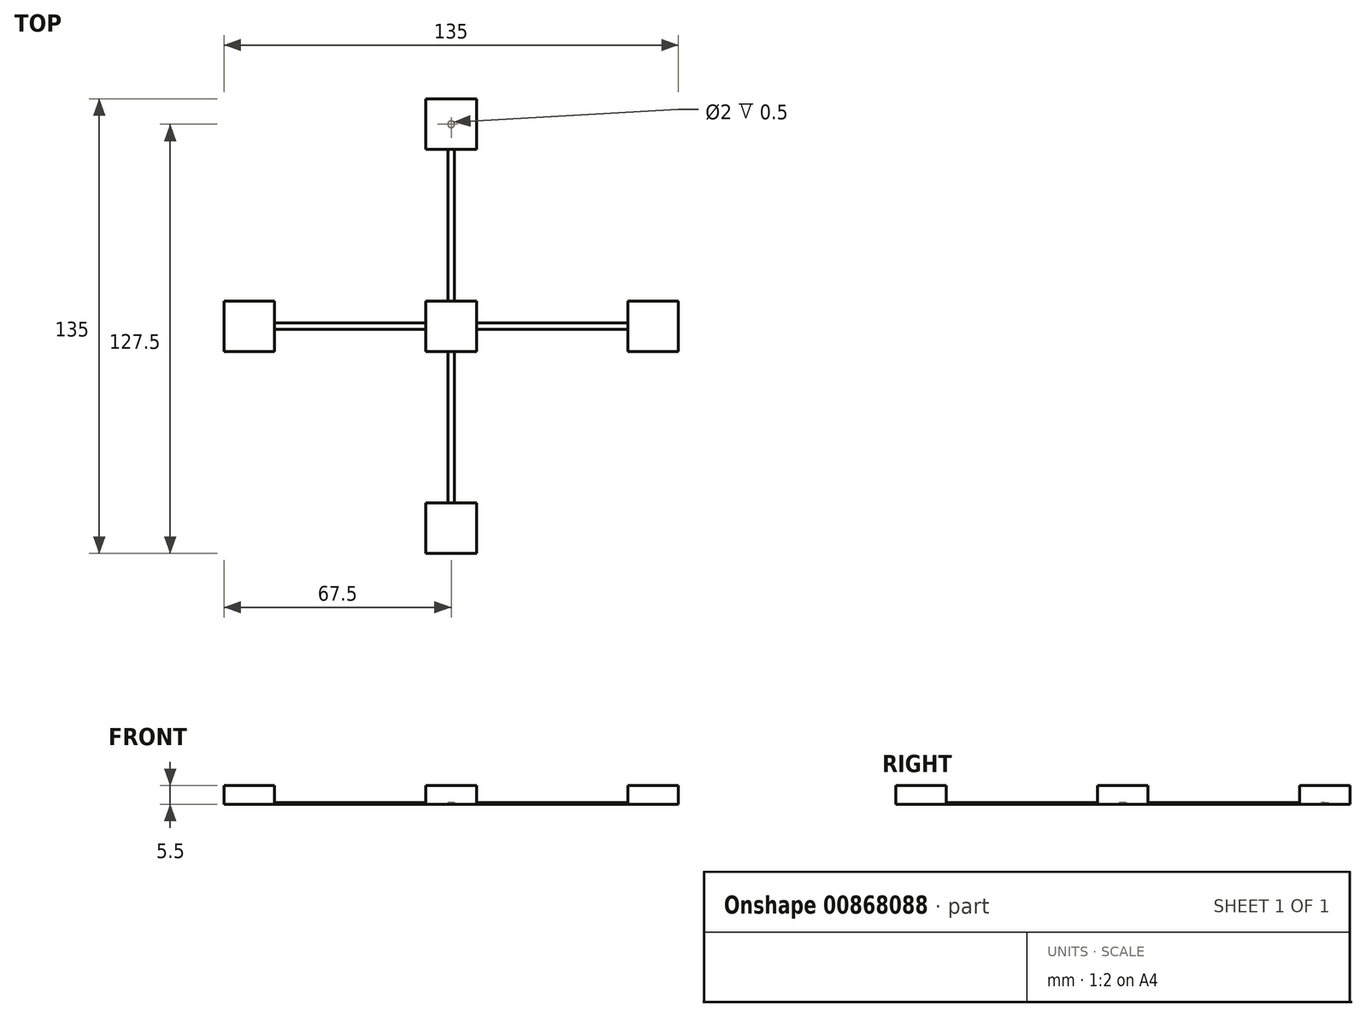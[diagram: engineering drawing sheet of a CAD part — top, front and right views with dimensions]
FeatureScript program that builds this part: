
annotation { "Feature Type Name" : "Feature", "Feature Type Description" : "" }
export const myFeature = defineFeature(function(context is Context, id is Id, definition is map)
    precondition{}
    {
        {
            var Q0;
            Q0=qCreatedBy(makeId("Top.planeOp"),FACE);
            var sketch = newSketch(context, id + "F0", { "sketchPlane" : qUnion([Q0])});
            skLineSegment(sketch, "E0.bottom", {"start": v(0, 0) * mm, "end": v(7.5, 0) * mm, "construction": true});
            skLineSegment(sketch, "E0.top", {"start": v(0, 7.5) * mm, "end": v(7.5, 7.5) * mm, "construction": true});
            skLineSegment(sketch, "E0.left", {"start": v(0, 0) * mm, "end": v(0, 7.5) * mm, "construction": true});
            skLineSegment(sketch, "E0.right", {"start": v(7.5, 0) * mm, "end": v(7.5, 7.5) * mm, "construction": true});
            skLineSegment(sketch, "E1.bottom", {"start": v(0, 67.5) * mm, "end": v(7.5, 67.5) * mm});
            skLineSegment(sketch, "E1.top", {"start": v(0, 52.5) * mm, "end": v(7.5, 52.5) * mm, "construction": true});
            skLineSegment(sketch, "E1.left", {"start": v(0, 67.5) * mm, "end": v(0, 52.5) * mm, "construction": true});
            skLineSegment(sketch, "E1.right", {"start": v(7.5, 67.5) * mm, "end": v(7.5, 52.5) * mm});
            skLineSegment(sketch, "E2", {"start": v(0, 0) * mm, "end": v(7.5, 7.5) * mm, "construction": true});
            skLineSegment(sketch, "E3", {"start": v(7.5, 52.5) * mm, "end": v(1, 52.5) * mm});
            skLineSegment(sketch, "E4", {"start": v(1, 52.5) * mm, "end": v(1, 7.5) * mm});
            skLineSegment(sketch, "E5", {"start": v(1, 7.5) * mm, "end": v(7.5, 7.5) * mm});
            skLineSegment(sketch, "E6.MirrorCS", {"start": v(52.5, 7.5) * mm, "end": v(52.5, 1) * mm});
            skLineSegment(sketch, "E7.MirrorCS", {"start": v(7.5, 1) * mm, "end": v(7.5, 7.5) * mm});
            skLineSegment(sketch, "E8.MirrorCS", {"start": v(52.5, 1) * mm, "end": v(7.5, 1) * mm});
            skLineSegment(sketch, "E9.MirrorCS", {"start": v(52.5, 0) * mm, "end": v(52.5, 7.5) * mm, "construction": true});
            skLineSegment(sketch, "E10.MirrorCS", {"start": v(67.5, 0) * mm, "end": v(52.5, 0) * mm, "construction": true});
            skLineSegment(sketch, "E11.MirrorCS", {"start": v(67.5, 7.5) * mm, "end": v(52.5, 7.5) * mm});
            skLineSegment(sketch, "E12.MirrorCS", {"start": v(67.5, 0) * mm, "end": v(67.5, 7.5) * mm});
            skLineSegment(sketch, "E13.1.0", {"start": v(0, 0) * mm, "end": v(-7.5, 7.5) * mm, "construction": true});
            skLineSegment(sketch, "E13.1.1", {"start": v(0, 52.5) * mm, "end": v(-7.5, 52.5) * mm, "construction": true});
            skLineSegment(sketch, "E13.1.2", {"start": v(-1, 52.5) * mm, "end": v(-1, 7.5) * mm});
            skLineSegment(sketch, "E13.1.3", {"start": v(0, 0) * mm, "end": v(-7.5, 0) * mm, "construction": true});
            skLineSegment(sketch, "E13.1.4", {"start": v(-67.5, 0) * mm, "end": v(-52.5, 0) * mm, "construction": true});
            skLineSegment(sketch, "E13.1.5", {"start": v(-52.5, 0) * mm, "end": v(-52.5, 7.5) * mm, "construction": true});
            skLineSegment(sketch, "E13.1.7", {"start": v(-7.5, 0) * mm, "end": v(-7.5, 7.5) * mm, "construction": true});
            skLineSegment(sketch, "E13.1.8", {"start": v(-52.5, 1) * mm, "end": v(-7.5, 1) * mm});
            skLineSegment(sketch, "E13.1.9", {"start": v(0, 7.5) * mm, "end": v(-7.5, 7.5) * mm, "construction": true});
            skLineSegment(sketch, "E13.1.10", {"start": v(0, 67.5) * mm, "end": v(-7.5, 67.5) * mm});
            skLineSegment(sketch, "E13.1.11", {"start": v(-7.5, 67.5) * mm, "end": v(-7.5, 52.5) * mm});
            skLineSegment(sketch, "E13.1.12", {"start": v(-67.5, 0) * mm, "end": v(-67.5, 7.5) * mm});
            skLineSegment(sketch, "E13.1.14", {"start": v(-67.5, 7.5) * mm, "end": v(-52.5, 7.5) * mm});
            skLineSegment(sketch, "E13.1.15", {"start": v(-7.5, 1) * mm, "end": v(-7.5, 7.5) * mm});
            skLineSegment(sketch, "E13.1.16", {"start": v(0, 7.5) * mm, "end": v(-7.5, 7.5) * mm, "construction": true});
            skLineSegment(sketch, "E13.1.17", {"start": v(-52.5, 7.5) * mm, "end": v(-52.5, 1) * mm});
            skLineSegment(sketch, "E13.1.18", {"start": v(-7.5, 52.5) * mm, "end": v(-1, 52.5) * mm});
            skLineSegment(sketch, "E13.1.19", {"start": v(-1, 7.5) * mm, "end": v(-7.5, 7.5) * mm});
            skLineSegment(sketch, "E13.2.0", {"start": v(0, 0) * mm, "end": v(-7.5, -7.5) * mm, "construction": true});
            skLineSegment(sketch, "E13.2.1", {"start": v(-52.5, 0) * mm, "end": v(-52.5, -7.5) * mm, "construction": true});
            skLineSegment(sketch, "E13.2.2", {"start": v(-52.5, -1) * mm, "end": v(-7.5, -1) * mm});
            skLineSegment(sketch, "E13.2.3", {"start": v(0, 0) * mm, "end": v(0, -7.5) * mm, "construction": true});
            skLineSegment(sketch, "E13.2.4", {"start": v(0, -67.5) * mm, "end": v(0, -52.5) * mm, "construction": true});
            skLineSegment(sketch, "E13.2.5", {"start": v(0, -52.5) * mm, "end": v(-7.5, -52.5) * mm, "construction": true});
            skLineSegment(sketch, "E13.2.6", {"start": v(0, 0) * mm, "end": v(-7.5, 0) * mm, "construction": true});
            skLineSegment(sketch, "E13.2.7", {"start": v(0, -7.5) * mm, "end": v(-7.5, -7.5) * mm, "construction": true});
            skLineSegment(sketch, "E13.2.8", {"start": v(-1, -52.5) * mm, "end": v(-1, -7.5) * mm});
            skLineSegment(sketch, "E13.2.9", {"start": v(-7.5, 0) * mm, "end": v(-7.5, -7.5) * mm, "construction": true});
            skLineSegment(sketch, "E13.2.10", {"start": v(-67.5, 0) * mm, "end": v(-67.5, -7.5) * mm});
            skLineSegment(sketch, "E13.2.11", {"start": v(-67.5, -7.5) * mm, "end": v(-52.5, -7.5) * mm});
            skLineSegment(sketch, "E13.2.12", {"start": v(0, -67.5) * mm, "end": v(-7.5, -67.5) * mm});
            skLineSegment(sketch, "E13.2.13", {"start": v(-67.5, 0) * mm, "end": v(-52.5, 0) * mm, "construction": true});
            skLineSegment(sketch, "E13.2.14", {"start": v(-7.5, -67.5) * mm, "end": v(-7.5, -52.5) * mm});
            skLineSegment(sketch, "E13.2.15", {"start": v(-1, -7.5) * mm, "end": v(-7.5, -7.5) * mm});
            skLineSegment(sketch, "E13.2.16", {"start": v(-7.5, 0) * mm, "end": v(-7.5, -7.5) * mm, "construction": true});
            skLineSegment(sketch, "E13.2.17", {"start": v(-7.5, -52.5) * mm, "end": v(-1, -52.5) * mm});
            skLineSegment(sketch, "E13.2.18", {"start": v(-52.5, -7.5) * mm, "end": v(-52.5, -1) * mm});
            skLineSegment(sketch, "E13.2.19", {"start": v(-7.5, -1) * mm, "end": v(-7.5, -7.5) * mm});
            skLineSegment(sketch, "E13.3.0", {"start": v(0, 0) * mm, "end": v(7.5, -7.5) * mm, "construction": true});
            skLineSegment(sketch, "E13.3.1", {"start": v(0, -52.5) * mm, "end": v(7.5, -52.5) * mm, "construction": true});
            skLineSegment(sketch, "E13.3.2", {"start": v(1, -52.5) * mm, "end": v(1, -7.5) * mm});
            skLineSegment(sketch, "E13.3.5", {"start": v(52.5, 0) * mm, "end": v(52.5, -7.5) * mm, "construction": true});
            skLineSegment(sketch, "E13.3.6", {"start": v(0, 0) * mm, "end": v(0, -7.5) * mm, "construction": true});
            skLineSegment(sketch, "E13.3.7", {"start": v(7.5, 0) * mm, "end": v(7.5, -7.5) * mm, "construction": true});
            skLineSegment(sketch, "E13.3.8", {"start": v(52.5, -1) * mm, "end": v(7.5, -1) * mm});
            skLineSegment(sketch, "E13.3.9", {"start": v(0, -7.5) * mm, "end": v(7.5, -7.5) * mm, "construction": true});
            skLineSegment(sketch, "E13.3.10", {"start": v(0, -67.5) * mm, "end": v(7.5, -67.5) * mm});
            skLineSegment(sketch, "E13.3.11", {"start": v(7.5, -67.5) * mm, "end": v(7.5, -52.5) * mm});
            skLineSegment(sketch, "E13.3.12", {"start": v(67.5, 0) * mm, "end": v(67.5, -7.5) * mm});
            skLineSegment(sketch, "E13.3.13", {"start": v(0, -67.5) * mm, "end": v(0, -52.5) * mm, "construction": true});
            skLineSegment(sketch, "E13.3.14", {"start": v(67.5, -7.5) * mm, "end": v(52.5, -7.5) * mm});
            skLineSegment(sketch, "E13.3.15", {"start": v(7.5, -1) * mm, "end": v(7.5, -7.5) * mm});
            skLineSegment(sketch, "E13.3.16", {"start": v(0, -7.5) * mm, "end": v(7.5, -7.5) * mm, "construction": true});
            skLineSegment(sketch, "E13.3.17", {"start": v(52.5, -7.5) * mm, "end": v(52.5, -1) * mm});
            skLineSegment(sketch, "E13.3.18", {"start": v(7.5, -52.5) * mm, "end": v(1, -52.5) * mm});
            skLineSegment(sketch, "E13.3.19", {"start": v(1, -7.5) * mm, "end": v(7.5, -7.5) * mm});
            skPoint(sketch, "E13.center", {"position": v(0, 0) * mm});
            skSolve(sketch);
        }
        {
            var Q0;
            Q0 = qSketchRegion(id + "F0", true);
            extrude(context, id + "F1", {"entities" : qUnion([Q0]), "depth" : 0.5 * mm, "offsetDistance" : 25 * mm});
        }
        {
            var Q0;
            Q0=makeQuery(id+"F1.opExtrude","CAP_FACE",FACE,{"disambiguationData":[OSD([sQuery(id+"F0.wireOp",EDGE,"E1.bottom"),sQuery(id+"F0.wireOp",EDGE,"E1.right"),sQuery(id+"F0.wireOp",EDGE,"E3"),sQuery(id+"F0.wireOp",EDGE,"E4"),sQuery(id+"F0.wireOp",EDGE,"E5"),sQuery(id+"F0.wireOp",EDGE,"E6.MirrorCS"),sQuery(id+"F0.wireOp",EDGE,"E7.MirrorCS"),sQuery(id+"F0.wireOp",EDGE,"E8.MirrorCS"),sQuery(id+"F0.wireOp",EDGE,"E11.MirrorCS"),sQuery(id+"F0.wireOp",EDGE,"E12.MirrorCS"),sQuery(id+"F0.wireOp",EDGE,"E13.1.2"),sQuery(id+"F0.wireOp",EDGE,"E13.1.8"),sQuery(id+"F0.wireOp",EDGE,"E13.1.10"),sQuery(id+"F0.wireOp",EDGE,"E13.1.11"),sQuery(id+"F0.wireOp",EDGE,"E13.1.12"),sQuery(id+"F0.wireOp",EDGE,"E13.1.14"),sQuery(id+"F0.wireOp",EDGE,"E13.1.15"),sQuery(id+"F0.wireOp",EDGE,"E13.1.17"),sQuery(id+"F0.wireOp",EDGE,"E13.1.18"),sQuery(id+"F0.wireOp",EDGE,"E13.1.19"),sQuery(id+"F0.wireOp",EDGE,"E13.2.2"),sQuery(id+"F0.wireOp",EDGE,"E13.2.8"),sQuery(id+"F0.wireOp",EDGE,"E13.2.10"),sQuery(id+"F0.wireOp",EDGE,"E13.2.11"),sQuery(id+"F0.wireOp",EDGE,"E13.2.12"),sQuery(id+"F0.wireOp",EDGE,"E13.2.14"),sQuery(id+"F0.wireOp",EDGE,"E13.2.15"),sQuery(id+"F0.wireOp",EDGE,"E13.2.17"),sQuery(id+"F0.wireOp",EDGE,"E13.2.18"),sQuery(id+"F0.wireOp",EDGE,"E13.2.19"),sQuery(id+"F0.wireOp",EDGE,"E13.3.2"),sQuery(id+"F0.wireOp",EDGE,"E13.3.8"),sQuery(id+"F0.wireOp",EDGE,"E13.3.10"),sQuery(id+"F0.wireOp",EDGE,"E13.3.11"),sQuery(id+"F0.wireOp",EDGE,"E13.3.12"),sQuery(id+"F0.wireOp",EDGE,"E13.3.14"),sQuery(id+"F0.wireOp",EDGE,"E13.3.15"),sQuery(id+"F0.wireOp",EDGE,"E13.3.17"),sQuery(id+"F0.wireOp",EDGE,"E13.3.18"),sQuery(id+"F0.wireOp",EDGE,"E13.3.19")])],"isStart":true});
            var sketch = newSketch(context, id + "F2", { "sketchPlane" : qUnion([Q0])});
            skLineSegment(sketch, "E14", {"start": v(7.5, -52.5) * mm, "end": v(-7.5, -67.5) * mm, "construction": true});
            skCircle(sketch, "E15", {"center": v(0, -60) * mm, "radius": 1 * mm});
            skSolve(sketch);
        }
        {
            var Q0;
            Q0 = qSketchRegion(id + "F2", true);
            var Q1;
            Q1=makeQuery(id+"F1.opExtrude","CAP_FACE",FACE,{"disambiguationData":[OSD([sQuery(id+"F0.wireOp",EDGE,"E1.bottom"),sQuery(id+"F0.wireOp",EDGE,"E1.right"),sQuery(id+"F0.wireOp",EDGE,"E3"),sQuery(id+"F0.wireOp",EDGE,"E4"),sQuery(id+"F0.wireOp",EDGE,"E5"),sQuery(id+"F0.wireOp",EDGE,"E6.MirrorCS"),sQuery(id+"F0.wireOp",EDGE,"E7.MirrorCS"),sQuery(id+"F0.wireOp",EDGE,"E8.MirrorCS"),sQuery(id+"F0.wireOp",EDGE,"E11.MirrorCS"),sQuery(id+"F0.wireOp",EDGE,"E12.MirrorCS"),sQuery(id+"F0.wireOp",EDGE,"E13.1.2"),sQuery(id+"F0.wireOp",EDGE,"E13.1.8"),sQuery(id+"F0.wireOp",EDGE,"E13.1.10"),sQuery(id+"F0.wireOp",EDGE,"E13.1.11"),sQuery(id+"F0.wireOp",EDGE,"E13.1.12"),sQuery(id+"F0.wireOp",EDGE,"E13.1.14"),sQuery(id+"F0.wireOp",EDGE,"E13.1.15"),sQuery(id+"F0.wireOp",EDGE,"E13.1.17"),sQuery(id+"F0.wireOp",EDGE,"E13.1.18"),sQuery(id+"F0.wireOp",EDGE,"E13.1.19"),sQuery(id+"F0.wireOp",EDGE,"E13.2.2"),sQuery(id+"F0.wireOp",EDGE,"E13.2.8"),sQuery(id+"F0.wireOp",EDGE,"E13.2.10"),sQuery(id+"F0.wireOp",EDGE,"E13.2.11"),sQuery(id+"F0.wireOp",EDGE,"E13.2.12"),sQuery(id+"F0.wireOp",EDGE,"E13.2.14"),sQuery(id+"F0.wireOp",EDGE,"E13.2.15"),sQuery(id+"F0.wireOp",EDGE,"E13.2.17"),sQuery(id+"F0.wireOp",EDGE,"E13.2.18"),sQuery(id+"F0.wireOp",EDGE,"E13.2.19"),sQuery(id+"F0.wireOp",EDGE,"E13.3.2"),sQuery(id+"F0.wireOp",EDGE,"E13.3.8"),sQuery(id+"F0.wireOp",EDGE,"E13.3.10"),sQuery(id+"F0.wireOp",EDGE,"E13.3.11"),sQuery(id+"F0.wireOp",EDGE,"E13.3.12"),sQuery(id+"F0.wireOp",EDGE,"E13.3.14"),sQuery(id+"F0.wireOp",EDGE,"E13.3.15"),sQuery(id+"F0.wireOp",EDGE,"E13.3.17"),sQuery(id+"F0.wireOp",EDGE,"E13.3.18"),sQuery(id+"F0.wireOp",EDGE,"E13.3.19")])],"isStart":false});
            extrude(context, id + "F3", {"entities" : qUnion([Q0]), "operationType" : NewBodyOperationType.REMOVE, "endBound" : BoundingType.UP_TO_SURFACE, "oppositeDirection" : true, "depth" : 25 * mm, "endBoundEntityFace" : qUnion([Q1]), "offsetDistance" : 25 * mm});
        }
        {
            var Q0;
            Q0=makeQuery(id+"F1.opExtrude","CAP_FACE",FACE,{"disambiguationData":[OSD([sQuery(id+"F0.wireOp",EDGE,"E1.bottom"),sQuery(id+"F0.wireOp",EDGE,"E1.right"),sQuery(id+"F0.wireOp",EDGE,"E3"),sQuery(id+"F0.wireOp",EDGE,"E4"),sQuery(id+"F0.wireOp",EDGE,"E5"),sQuery(id+"F0.wireOp",EDGE,"E6.MirrorCS"),sQuery(id+"F0.wireOp",EDGE,"E7.MirrorCS"),sQuery(id+"F0.wireOp",EDGE,"E8.MirrorCS"),sQuery(id+"F0.wireOp",EDGE,"E11.MirrorCS"),sQuery(id+"F0.wireOp",EDGE,"E12.MirrorCS"),sQuery(id+"F0.wireOp",EDGE,"E13.1.2"),sQuery(id+"F0.wireOp",EDGE,"E13.1.8"),sQuery(id+"F0.wireOp",EDGE,"E13.1.10"),sQuery(id+"F0.wireOp",EDGE,"E13.1.11"),sQuery(id+"F0.wireOp",EDGE,"E13.1.12"),sQuery(id+"F0.wireOp",EDGE,"E13.1.14"),sQuery(id+"F0.wireOp",EDGE,"E13.1.15"),sQuery(id+"F0.wireOp",EDGE,"E13.1.17"),sQuery(id+"F0.wireOp",EDGE,"E13.1.18"),sQuery(id+"F0.wireOp",EDGE,"E13.1.19"),sQuery(id+"F0.wireOp",EDGE,"E13.2.2"),sQuery(id+"F0.wireOp",EDGE,"E13.2.8"),sQuery(id+"F0.wireOp",EDGE,"E13.2.10"),sQuery(id+"F0.wireOp",EDGE,"E13.2.11"),sQuery(id+"F0.wireOp",EDGE,"E13.2.12"),sQuery(id+"F0.wireOp",EDGE,"E13.2.14"),sQuery(id+"F0.wireOp",EDGE,"E13.2.15"),sQuery(id+"F0.wireOp",EDGE,"E13.2.17"),sQuery(id+"F0.wireOp",EDGE,"E13.2.18"),sQuery(id+"F0.wireOp",EDGE,"E13.2.19"),sQuery(id+"F0.wireOp",EDGE,"E13.3.2"),sQuery(id+"F0.wireOp",EDGE,"E13.3.8"),sQuery(id+"F0.wireOp",EDGE,"E13.3.10"),sQuery(id+"F0.wireOp",EDGE,"E13.3.11"),sQuery(id+"F0.wireOp",EDGE,"E13.3.12"),sQuery(id+"F0.wireOp",EDGE,"E13.3.14"),sQuery(id+"F0.wireOp",EDGE,"E13.3.15"),sQuery(id+"F0.wireOp",EDGE,"E13.3.17"),sQuery(id+"F0.wireOp",EDGE,"E13.3.18"),sQuery(id+"F0.wireOp",EDGE,"E13.3.19")])],"isStart":false});
            var sketch = newSketch(context, id + "F4", { "sketchPlane" : qUnion([Q0])});
            skLineSegment(sketch, "E16.bottom", {"start": v(-67.5, 7.5) * mm, "end": v(-52.5, 7.5) * mm});
            skLineSegment(sketch, "E16.top", {"start": v(-67.5, -7.5) * mm, "end": v(-52.5, -7.5) * mm});
            skLineSegment(sketch, "E16.left", {"start": v(-67.5, 7.5) * mm, "end": v(-67.5, -7.5) * mm});
            skLineSegment(sketch, "E16.right", {"start": v(-52.5, 7.5) * mm, "end": v(-52.5, -7.5) * mm});
            skLineSegment(sketch, "E17.bottom", {"start": v(-7.5, 67.5) * mm, "end": v(7.5, 67.5) * mm});
            skLineSegment(sketch, "E17.top", {"start": v(-7.5, 52.5) * mm, "end": v(7.5, 52.5) * mm});
            skLineSegment(sketch, "E17.left", {"start": v(-7.5, 67.5) * mm, "end": v(-7.5, 52.5) * mm});
            skLineSegment(sketch, "E17.right", {"start": v(7.5, 67.5) * mm, "end": v(7.5, 52.5) * mm});
            skLineSegment(sketch, "E18.bottom", {"start": v(52.5, 7.5) * mm, "end": v(67.5, 7.5) * mm});
            skLineSegment(sketch, "E18.top", {"start": v(52.5, -7.5) * mm, "end": v(67.5, -7.5) * mm});
            skLineSegment(sketch, "E18.left", {"start": v(52.5, 7.5) * mm, "end": v(52.5, -7.5) * mm});
            skLineSegment(sketch, "E18.right", {"start": v(67.5, 7.5) * mm, "end": v(67.5, -7.5) * mm});
            skLineSegment(sketch, "E19.bottom", {"start": v(-7.5, 7.5) * mm, "end": v(7.5, 7.5) * mm});
            skLineSegment(sketch, "E19.top", {"start": v(-7.5, -7.5) * mm, "end": v(7.5, -7.5) * mm});
            skLineSegment(sketch, "E19.left", {"start": v(-7.5, 7.5) * mm, "end": v(-7.5, -7.5) * mm});
            skLineSegment(sketch, "E19.right", {"start": v(7.5, 7.5) * mm, "end": v(7.5, -7.5) * mm});
            skLineSegment(sketch, "E20.bottom", {"start": v(-7.5, -52.5) * mm, "end": v(7.5, -52.5) * mm});
            skLineSegment(sketch, "E20.top", {"start": v(-7.5, -67.5) * mm, "end": v(7.5, -67.5) * mm});
            skLineSegment(sketch, "E20.left", {"start": v(-7.5, -52.5) * mm, "end": v(-7.5, -67.5) * mm});
            skLineSegment(sketch, "E20.right", {"start": v(7.5, -52.5) * mm, "end": v(7.5, -67.5) * mm});
            skSolve(sketch);
        }
        {
            var Q0;
            Q0 = qSketchRegion(id + "F4", true);
            extrude(context, id + "F5", {"entities" : qUnion([Q0]), "operationType" : NewBodyOperationType.ADD, "depth" : 5 * mm, "offsetDistance" : 25 * mm});
        }
    });
